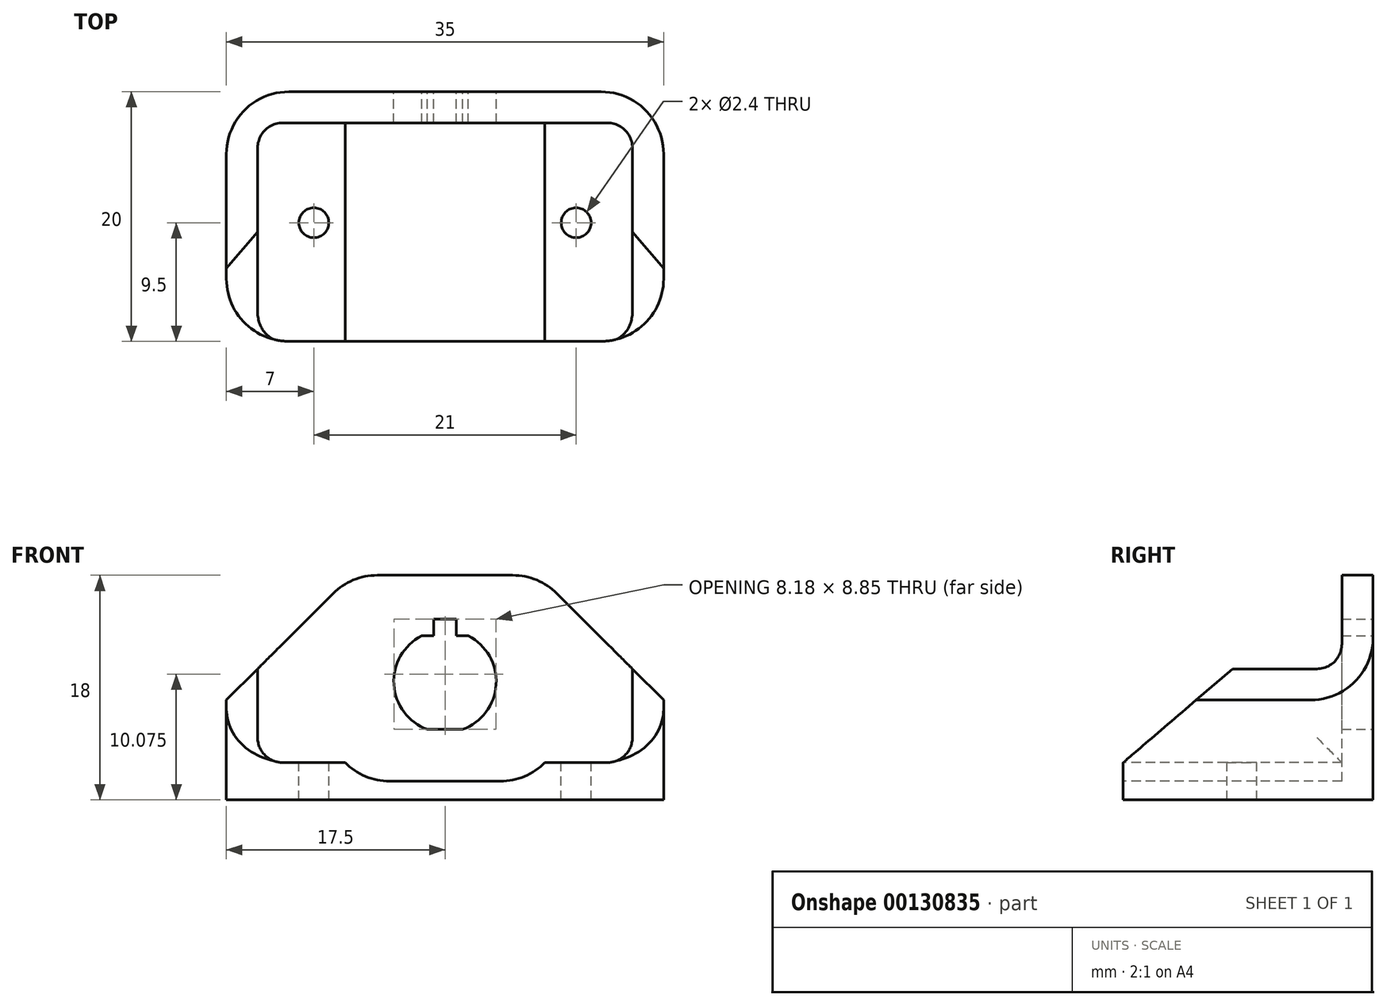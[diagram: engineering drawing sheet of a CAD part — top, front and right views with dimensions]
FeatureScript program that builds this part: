
annotation { "Feature Type Name" : "Feature", "Feature Type Description" : "" }
export const myFeature = defineFeature(function(context is Context, id is Id, definition is map)
    precondition{}
    {
        {
            var Q0;
            Q0=qCreatedBy(makeId("Front.planeOp"),FACE);
            var sketch = newSketch(context, id + "F0", { "sketchPlane" : qUnion([Q0])});
            skLineSegment(sketch, "E0.bottom", {"start": v(17.5, 18) * mm, "end": v(-17.5, 18) * mm});
            skLineSegment(sketch, "E0.top", {"start": v(17.5, 0) * mm, "end": v(-17.5, 0) * mm});
            skLineSegment(sketch, "E0.left", {"start": v(17.5, 18) * mm, "end": v(17.5, 0) * mm});
            skLineSegment(sketch, "E0.right", {"start": v(-17.5, 18) * mm, "end": v(-17.5, 0) * mm});
            skPoint(sketch, "E0.middle", {"position": v(0, 9) * mm});
            skSolve(sketch);
        }
        {
            var Q0;
            Q0=makeQuery(id+"F0.imprint","IMPRINT",FACE,{"disambiguationData":[TD([[makeQuery(id+"F0.imprint","IMPRINT",EDGE,{"derivedFrom":sQuery(id+"F0.wireOp",EDGE,"E0.bottom")}),1.0]])]});
            extrude(context, id + "F1", {"entities" : qUnion([Q0]), "depth" : 20 * mm});
        }
        {
            var Q0;
            Q0=makeQuery(id+"F1.opExtrude","SWEPT_FACE",FACE,{"disambiguationData":[OSD([sQuery(id+"F0.wireOp",EDGE,"E0.bottom")])]});
            var sketch = newSketch(context, id + "F2", { "sketchPlane" : qUnion([Q0])});
            skLineSegment(sketch, "E1.bottom", {"start": v(-15, -2.5) * mm, "end": v(15, -2.5) * mm});
            skLineSegment(sketch, "E1.top", {"start": v(-15, -26.2) * mm, "end": v(15, -26.2) * mm});
            skLineSegment(sketch, "E1.left", {"start": v(-15, -2.5) * mm, "end": v(-15, -26.2) * mm});
            skLineSegment(sketch, "E1.right", {"start": v(15, -2.5) * mm, "end": v(15, -26.2) * mm});
            skSolve(sketch);
        }
        {
            var Q0;
            Q0 = qSketchRegion(id + "F2", true);
            extrude(context, id + "F3", {"entities" : qUnion([Q0]), "operationType" : NewBodyOperationType.REMOVE, "oppositeDirection" : true, "depth" : 15 * mm});
        }
        {
            var Q0;
            Q0=makeQuery(id+"F3.boolean.opBoolean","COPY",FACE,{"derivedFrom":makeQuery(id+"F3.opExtrude","SWEPT_FACE",FACE,{"disambiguationData":[OSD([sQuery(id+"F2.wireOp",EDGE,"E1.right")])]})});
            var sketch = newSketch(context, id + "F4", { "sketchPlane" : qUnion([Q0])});
            skLineSegment(sketch, "E2", {"start": v(2.5, 18) * mm, "end": v(20, 3) * mm});
            skLineSegment(sketch, "E3", {"start": v(20, 3) * mm, "end": v(20, 18) * mm});
            skLineSegment(sketch, "E4", {"start": v(20, 18) * mm, "end": v(2.5, 18) * mm});
            skSolve(sketch);
        }
        {
            var Q0;
            Q0 = qSketchRegion(id + "F4", true);
            extrude(context, id + "F5", {"entities" : qUnion([Q0]), "operationType" : NewBodyOperationType.REMOVE, "endBound" : BoundingType.SYMMETRIC, "depth" : 65 * mm});
        }
        {
            var Q0;
            Q0=makeQuery(id+"F1.opExtrude","SWEPT_EDGE",EDGE,{"disambiguationData":[OSD([sQuery(id+"F0.wireOp",EDGE,"E0.bottom"),sQuery(id+"F0.wireOp",EDGE,"E0.left")])]});
            var Q1;
            Q1=makeQuery(id+"F1.opExtrude","SWEPT_EDGE",EDGE,{"disambiguationData":[OSD([sQuery(id+"F0.wireOp",EDGE,"E0.bottom"),sQuery(id+"F0.wireOp",EDGE,"E0.right")])]});
            chamfer(context, id + "F6", {"entities" : qUnion([Q0, Q1]), "width" : 10 * mm, "tangentPropagation" : true});
        }
        {
            var Q0;
            Q0=makeQuery(id+"F3.boolean.opBoolean","COPY",EDGE,{"derivedFrom":makeQuery(id+"F3.opExtrude","SWEPT_EDGE",EDGE,{"disambiguationData":[OSD([sQuery(id+"F2.wireOp",EDGE,"E1.bottom"),sQuery(id+"F2.wireOp",EDGE,"E1.left")])]})});
            var Q1;
            Q1=makeQuery(id+"F3.boolean.opBoolean","COPY",EDGE,{"derivedFrom":makeQuery(id+"F3.opExtrude","SWEPT_EDGE",EDGE,{"disambiguationData":[OSD([sQuery(id+"F2.wireOp",EDGE,"E1.bottom"),sQuery(id+"F2.wireOp",EDGE,"E1.right")])]})});
            var Q2;
            Q2=makeQuery(id+"F3.boolean.opBoolean","COPY",EDGE,{"derivedFrom":makeQuery(id+"F3.opExtrude","CAP_EDGE",EDGE,{"disambiguationData":[OSD([sQuery(id+"F2.wireOp",EDGE,"E1.left")])],"isStart":false})});
            var Q3;
            Q3=makeQuery(id+"F3.boolean.opBoolean","COPY",EDGE,{"derivedFrom":makeQuery(id+"F3.opExtrude","CAP_EDGE",EDGE,{"disambiguationData":[OSD([sQuery(id+"F2.wireOp",EDGE,"E1.right")])],"isStart":false})});
            fillet(context, id + "F7", {"entities" : qUnion([Q0, Q1, Q2, Q3]), "radius" : 2 * mm, "tangentPropagation" : true, "allowEdgeOverflow" : false});
        }
        {
            var Q0;
            Q0=makeQuery(id+"F1.opExtrude","CAP_FACE",FACE,{"disambiguationData":[OSD([sQuery(id+"F0.wireOp",EDGE,"E0.bottom"),sQuery(id+"F0.wireOp",EDGE,"E0.top"),sQuery(id+"F0.wireOp",EDGE,"E0.left"),sQuery(id+"F0.wireOp",EDGE,"E0.right")])],"isStart":true});
            var sketch = newSketch(context, id + "F8", { "sketchPlane" : qUnion([Q0])});
            skArc(sketch, "E5", {"start": v(1.4, 5.65) * mm, "mid": v(4.1, 9.25) * mm, "end": v(1.87, 13.15) * mm});
            skLineSegment(sketch, "E6.bottom", {"start": v(0.9, 14.5) * mm, "end": v(-0.9, 14.5) * mm});
            skLineSegment(sketch, "E6.left", {"start": v(0.9, 14.5) * mm, "end": v(0.9, 13.15) * mm});
            skLineSegment(sketch, "E6.right", {"start": v(-0.9, 14.5) * mm, "end": v(-0.9, 13.15) * mm});
            skPoint(sketch, "E6.middle", {"position": v(0, 13.6) * mm});
            skLineSegment(sketch, "E7", {"start": v(-1.4, 5.65) * mm, "end": v(1.4, 5.65) * mm});
            skLineSegment(sketch, "E8", {"start": v(-1.87, 13.15) * mm, "end": v(-0.9, 13.15) * mm});
            skPoint(sketch, "E9.orphan", {"position": v(-0.9, 12.7) * mm});
            skPoint(sketch, "E10.orphan", {"position": v(0.9, 12.7) * mm});
            skArc(sketch, "E11.trimOffspring", {"start": v(-1.87, 13.15) * mm, "mid": v(-4.1, 9.25) * mm, "end": v(-1.4, 5.65) * mm});
            skLineSegment(sketch, "E12.trimOffspring", {"start": v(0.9, 13.15) * mm, "end": v(1.87, 13.15) * mm});
            skSolve(sketch);
        }
        {
            var Q0;
            Q0=qCreatedBy(makeId("Front.planeOp"),FACE);
            var sketch = newSketch(context, id + "F9", { "sketchPlane" : qUnion([Q0])});
            skSolve(sketch);
        }
        {
            var Q0;
            Q0 = qSketchRegion(id + "F9", true);
            var Q1;
            Q1=makeQuery(id+"F8.imprint","IMPRINT",FACE,{"disambiguationData":[TD([[makeQuery(id+"F8.imprint","IMPRINT",EDGE,{"derivedFrom":sQuery(id+"F8.wireOp",EDGE,"E5")}),1.0]])]});
            extrude(context, id + "F10", {"entities" : qUnion([Q0, Q1]), "operationType" : NewBodyOperationType.REMOVE, "oppositeDirection" : true, "depth" : 25 * mm});
        }
        {
            var Q0;
            {var subQ0=sQuery(id+"F0.wireOp",EDGE,"E0.bottom");Q0=makeQuery(id+"F6.opChamfer","BLEND_EDGE",EDGE,{"blendedFrom":[makeQuery(id+"F1.opExtrude","SWEPT_EDGE",EDGE,{"disambiguationData":[OSD([subQ0,sQuery(id+"F0.wireOp",EDGE,"E0.left")])]}),makeQuery(id+"F1.opExtrude","SWEPT_FACE",FACE,{"disambiguationData":[OSD([subQ0])]})],"blendedInto":[makeQuery(id+"F1.opExtrude","SWEPT_FACE",FACE,{"disambiguationData":[OSD([subQ0])]})]});}
            var Q1;
            {var subQ0=sQuery(id+"F0.wireOp",EDGE,"E0.bottom");Q1=makeQuery(id+"F6.opChamfer","BLEND_EDGE",EDGE,{"blendedFrom":[makeQuery(id+"F1.opExtrude","SWEPT_EDGE",EDGE,{"disambiguationData":[OSD([subQ0,sQuery(id+"F0.wireOp",EDGE,"E0.right")])]}),makeQuery(id+"F1.opExtrude","SWEPT_FACE",FACE,{"disambiguationData":[OSD([subQ0])]})],"blendedInto":[makeQuery(id+"F1.opExtrude","SWEPT_FACE",FACE,{"disambiguationData":[OSD([subQ0])]})]});}
            var Q2;
            Q2=makeQuery(id+"F1.opExtrude","CAP_EDGE",EDGE,{"disambiguationData":[OSD([sQuery(id+"F0.wireOp",EDGE,"E0.left")])],"isStart":true});
            var Q3;
            Q3=makeQuery(id+"F1.opExtrude","CAP_EDGE",EDGE,{"disambiguationData":[OSD([sQuery(id+"F0.wireOp",EDGE,"E0.right")])],"isStart":true});
            fillet(context, id + "F11", {"entities" : qUnion([Q0, Q1, Q2, Q3]), "radius" : 5 * mm, "tangentPropagation" : true, "allowEdgeOverflow" : false});
        }
        {
            var Q0;
            Q0=makeQuery(id+"F3.boolean.opBoolean","COPY",FACE,{"derivedFrom":makeQuery(id+"F3.opExtrude","CAP_FACE",FACE,{"disambiguationData":[OSD([sQuery(id+"F2.wireOp",EDGE,"E1.bottom"),sQuery(id+"F2.wireOp",EDGE,"E1.top"),sQuery(id+"F2.wireOp",EDGE,"E1.left"),sQuery(id+"F2.wireOp",EDGE,"E1.right")])],"isStart":false})});
            var sketch = newSketch(context, id + "F12", { "sketchPlane" : qUnion([Q0])});
            skLineSegment(sketch, "E13.bottom", {"start": v(8, -2.5) * mm, "end": v(-8, -2.5) * mm});
            skLineSegment(sketch, "E13.top", {"start": v(8, -25.5) * mm, "end": v(-8, -25.5) * mm});
            skLineSegment(sketch, "E13.left", {"start": v(8, -2.5) * mm, "end": v(8, -25.5) * mm});
            skLineSegment(sketch, "E13.right", {"start": v(-8, -2.5) * mm, "end": v(-8, -25.5) * mm});
            skPoint(sketch, "E13.middle", {"position": v(0, -14) * mm});
            skSolve(sketch);
        }
        {
            var Q0;
            {var subQ0=sQuery(id+"F12.wireOp",EDGE,"E13.bottom");Q0=makeQuery(id+"F12.imprint","IMPRINT",FACE,{"disambiguationData":[TD([[makeQuery(id+"F12.imprint","IMPRINT",EDGE,{"derivedFrom":subQ0}),-1.0]])]});}
            extrude(context, id + "F13", {"entities" : qUnion([Q0]), "operationType" : NewBodyOperationType.REMOVE, "oppositeDirection" : true, "depth" : 1.5 * mm});
        }
        {
            var Q0;
            Q0=makeQuery(id+"F13.boolean.opBoolean","COPY",EDGE,{"derivedFrom":makeQuery(id+"F13.opExtrude","CAP_EDGE",EDGE,{"disambiguationData":[OSD([sQuery(id+"F12.wireOp",EDGE,"E13.right")])],"isStart":false})});
            var Q1;
            Q1=makeQuery(id+"F13.boolean.opBoolean","COPY",EDGE,{"derivedFrom":makeQuery(id+"F13.opExtrude","CAP_EDGE",EDGE,{"disambiguationData":[OSD([sQuery(id+"F12.wireOp",EDGE,"E13.left")])],"isStart":false})});
            var Q2;
            Q2=makeQuery(id+"F1.opExtrude","CAP_EDGE",EDGE,{"disambiguationData":[OSD([sQuery(id+"F0.wireOp",EDGE,"E0.right")])],"isStart":false});
            var Q3;
            Q3=makeQuery(id+"F1.opExtrude","CAP_EDGE",EDGE,{"disambiguationData":[OSD([sQuery(id+"F0.wireOp",EDGE,"E0.left")])],"isStart":false});
            fillet(context, id + "F14", {"entities" : qUnion([Q0, Q1, Q2, Q3]), "radius" : 5 * mm, "tangentPropagation" : true, "allowEdgeOverflow" : false});
        }
        {
            var Q0;
            {var subQ0=sQuery(id+"F2.wireOp",EDGE,"E1.bottom");var subQ1=sQuery(id+"F2.wireOp",EDGE,"E1.left");Q0=makeQuery(id+"F13.boolean.opBoolean","SPLIT",FACE,{"disambiguationData":[TD([makeQuery(id+"F5.boolean.opBoolean","COPY",FACE,{"disambiguationData":[OD(0.0)],"derivedFrom":makeQuery(id+"F5.opExtrude","SWEPT_FACE",FACE,{"disambiguationData":[OSD([sQuery(id+"F4.wireOp",EDGE,"E2")])]})})])],"derivedFrom":makeQuery(id+"F3.boolean.opBoolean","COPY",FACE,{"derivedFrom":makeQuery(id+"F3.opExtrude","CAP_FACE",FACE,{"disambiguationData":[OSD([subQ0,sQuery(id+"F2.wireOp",EDGE,"E1.top"),subQ1,sQuery(id+"F2.wireOp",EDGE,"E1.right")])],"isStart":false})})});}
            var sketch = newSketch(context, id + "F15", { "sketchPlane" : qUnion([Q0])});
            skCircle(sketch, "E14", {"center": v(-10.5, -10.5) * mm, "radius": 1.2 * mm});
            skLineSegment(sketch, "E15", {"start": v(-10.5, -10.5) * mm, "end": v(10.5, -10.5) * mm});
            skCircle(sketch, "E16", {"center": v(10.5, -10.5) * mm, "radius": 1.2 * mm});
            skSolve(sketch);
        }
        {
            var Q0;
            Q0=makeQuery(id+"F15.imprint","IMPRINT",FACE,{"disambiguationData":[TD([[makeQuery(id+"F15.imprint","IMPRINT",EDGE,{"derivedFrom":sQuery(id+"F15.wireOp",EDGE,"E14")}),1.0]])]});
            var Q1;
            Q1=makeQuery(id+"F15.imprint","IMPRINT",FACE,{"disambiguationData":[TD([[makeQuery(id+"F15.imprint","IMPRINT",EDGE,{"derivedFrom":sQuery(id+"F15.wireOp",EDGE,"E16")}),1.0]])]});
            extrude(context, id + "F16", {"entities" : qUnion([Q0, Q1]), "operationType" : NewBodyOperationType.REMOVE, "endBound" : BoundingType.THROUGH_ALL, "oppositeDirection" : true, "depth" : 25 * mm});
        }
    });
